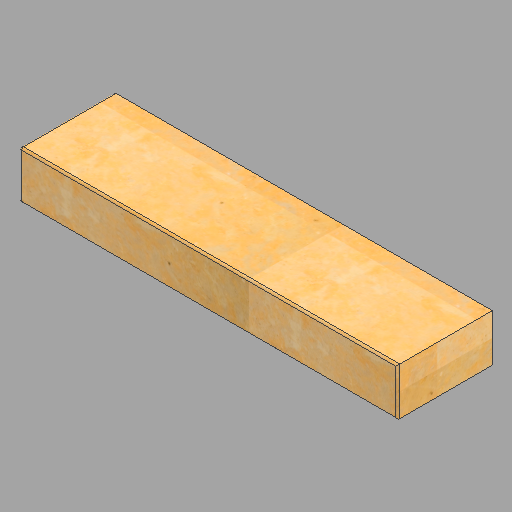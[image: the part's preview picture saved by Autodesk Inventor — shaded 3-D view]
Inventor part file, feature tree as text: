
AUTODESK INVENTOR PART (.ipt)
format: ipt  version: 2023 (Build 270158030, 158C)  size: 269,824 bytes
history: native  units: in
note: dims shown in document units (in); Inventor stores cm internally (conversion verified against a paired STEP export)
features: fillet x4, extrude x1, direct_edit x1, sketch x1, move_body x1
ambient origin geometry x8: Origin, YZ Plane, XZ Plane, XY Plane, X Axis, Y Axis, Z Axis, Center Point
bodies: Solid1 (feature_tree)
feature tree (8):
  extrude  "Extrusion1"  Depth=10.0in
  fillet  "Fillet2"  Radius=48.0in
  fillet  "Fillet3"  Radius=0.125in
  fillet  "Fillet4"  Radius=0.25in
  fillet  "Fillet5"  Radius=0.25in
  direct_edit  "Direct Edit1"
  sketch  "Sketch1"  dims[d0=6.0in d1=10.0in d2=48.0in d3=0.0in d12=0.125in d13=0.25in d14=0.25in d15=0.125in d16=0.0in d17=0.0in d18=2.0in]
  move_body  "Move1"
